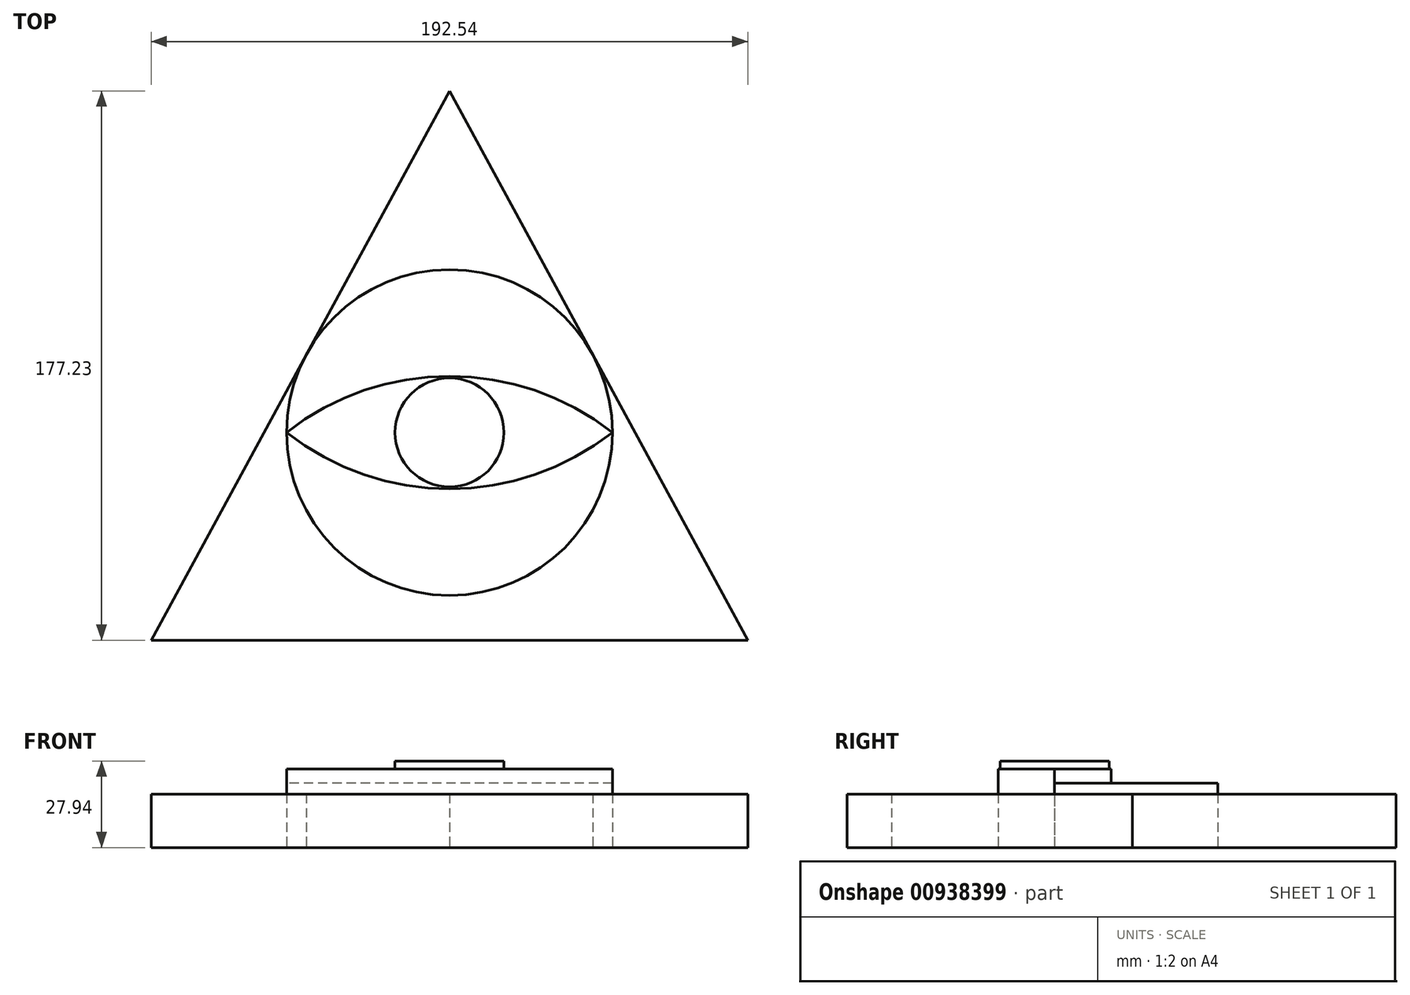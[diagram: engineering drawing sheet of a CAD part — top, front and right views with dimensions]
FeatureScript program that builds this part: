
annotation { "Feature Type Name" : "Feature", "Feature Type Description" : "" }
export const myFeature = defineFeature(function(context is Context, id is Id, definition is map)
    precondition{}
    {
        {
            var Q0;
            Q0=qCreatedBy(makeId("Top.planeOp"),FACE);
            var sketch = newSketch(context, id + "F0", { "sketchPlane" : qUnion([Q0])});
            skCircle(sketch, "E0", {"center": v(0, 0) * mm, "radius": 52.6 * mm});
            skArc(sketch, "E1", {"start": v(52.6, 0) * mm, "mid": v(0, 18.17) * mm, "end": v(-52.6, 0) * mm});
            skArc(sketch, "E2.MirrorCS", {"start": v(52.6, 0) * mm, "mid": v(0, -18.17) * mm, "end": v(-52.6, 0) * mm});
            skCircle(sketch, "E3", {"center": v(0, 0) * mm, "radius": 17.56 * mm});
            skLineSegment(sketch, "E4", {"start": v(0, 110.2) * mm, "end": v(-96.27, -67.03) * mm});
            skLineSegment(sketch, "E5", {"start": v(-96.27, -67.03) * mm, "end": v(0, -67.03) * mm});
            skLineSegment(sketch, "E6.MirrorCS", {"start": v(0, 110.2) * mm, "end": v(96.27, -67.03) * mm});
            skLineSegment(sketch, "E7.MirrorCS", {"start": v(96.27, -67.03) * mm, "end": v(0, -67.03) * mm});
            skSolve(sketch);
        }
        {
            var Q0;
            {var subQ0=sQuery(id+"F0.wireOp",EDGE,"E5");Q0=makeQuery(id+"F0.imprint","IMPRINT",FACE,{"disambiguationData":[TD([[makeQuery(id+"F0.imprint","IMPRINT",EDGE,{"derivedFrom":subQ0}),1.0]])]});}
            var Q1;
            {var subQ0=sQuery(id+"F0.wireOp",EDGE,"E6.MirrorCS");var subQ1=sQuery(id+"F0.wireOp",EDGE,"E0");var subQ2=makeQuery(id+"F0.imprint","INTERSECT",VERTEX,{"derivedFrom":[subQ1,subQ0]});Q1=makeQuery(id+"F0.imprint","IMPRINT",FACE,{"disambiguationData":[TD([[makeQuery(id+"F0.imprint","IMPRINT",EDGE,{"disambiguationData":[TD([[subQ2,-1.0]])],"derivedFrom":subQ1}),-1.0]])]});}
            extrude(context, id + "F1", {"entities" : qUnion([Q0, Q1]), "depth" : 17.27 * mm, "offsetDistance" : 25.4 * mm});
        }
        {
            var Q0;
            {var subQ1=sQuery(id+"F0.wireOp",EDGE,"E1");Q0=makeQuery(id+"F0.imprint","IMPRINT",FACE,{"disambiguationData":[TD([[makeQuery(id+"F0.imprint","IMPRINT",EDGE,{"derivedFrom":subQ1}),-1.0]])]});}
            var Q1;
            {var subQ0=sQuery(id+"F0.wireOp",EDGE,"E2.MirrorCS");Q1=makeQuery(id+"F0.imprint","IMPRINT",FACE,{"disambiguationData":[TD([[makeQuery(id+"F0.imprint","IMPRINT",EDGE,{"derivedFrom":subQ0}),1.0]])]});}
            extrude(context, id + "F2", {"entities" : qUnion([Q0, Q1]), "depth" : 20.83 * mm, "offsetDistance" : 25.4 * mm});
        }
        {
            var Q0;
            Q0=makeQuery(id+"F0.imprint","IMPRINT",FACE,{"disambiguationData":[TD([[makeQuery(id+"F0.imprint","IMPRINT",EDGE,{"derivedFrom":sQuery(id+"F0.wireOp",EDGE,"E1")}),1.0]])]});
            extrude(context, id + "F3", {"entities" : qUnion([Q0]), "depth" : 25.4 * mm, "offsetDistance" : 25.4 * mm});
        }
        {
            var Q0;
            Q0=makeQuery(id+"F0.imprint","IMPRINT",FACE,{"disambiguationData":[TD([[makeQuery(id+"F0.imprint","IMPRINT",EDGE,{"derivedFrom":sQuery(id+"F0.wireOp",EDGE,"E3")}),1.0]])]});
            extrude(context, id + "F4", {"entities" : qUnion([Q0]), "operationType" : NewBodyOperationType.ADD, "depth" : 27.94 * mm, "offsetDistance" : 25.4 * mm});
        }
    });
